# Revit family: Gira_277203
name_source: partatom
category: Elektroinstallationen
revit_build: Autodesk Revit 2017 (Build: 20160225_1515(x64)
units: mm (PartAtom-declared; Revit-internal decimal feet)

## family parameters
Basisbauteil = Fläche
Beim Laden mit Abzugskörper schneiden = Nein
Bemaßung runder Anschluss = Durchmesser verwenden
Beschriftungsausrichtung beibehalten = Nein
Gemeinsam genutzt = Nein
Raumberechnungspunkt = Nein
Teiletyp = Normal

## types (2) — shared parameters
Acoustic signal = Ja
Adjustable differential = Nein
Analogue input = Nein
Antibacterial treatment = Nein
BIM = https://media.stage.bim.site und Tasten.rfa
Beschreibung = Sock.BS Round Pin 5A SH Sys55 PW,Socket outlet British Standard (BS 546) Round Pin 5 A 250 V~ with shutter,System 55, Support ring 71 x 71 mm,pure white glossy,Features:,- With screw terminals.,- For screw mounting only.
Bus connection included = Nein
Bus system KNX = Ja
Bus system KNX radio = Nein
Bus system LON = Nein
Bus system Powernet = Nein
Bus system radio frequent = Nein
Colour = White
Connection = Two-wire
Connection type = Screwed terminal
Control characteristic = Other
Cooling = Nein
Data sheet = https://katalog.gira.de
Degree of protection (IP) = IP20
Eject-mechanism = Nein
Explosion-proof = Nein
External sensor = Nein
Fault current protection = Nein
Für "erschwerte Bedingungen" (nach VDE) (*de-DE) = Nein
GTIN = 4010337079095
HAN = 277203
Halogen free = Ja
Heating = Ja
Hersteller = Gira
Imprint/indication = Without imprint
Insulated mounting = Nein
Label space/information surface = Nein
Lockable = Nein
Material = Plastic
Material quality = Thermoplastic
Measuring range maximum value [m/s] = 30
Measuring range minimum value [m/s] = 5
Model = British Standard
Monitoring window/light outlet = Ja
Mounting method = Flush mounted (plaster)
Nominal current = 5 A
Nominal voltage [Volt] = 250
Number of channels = 3
Number of modules (module system) = 1
Number of units = 1
Operation = Turn
Other bus systems = None
Over voltage protection = Nein
Productwebsite = http://katalog.gira.de
Protective earth pin round = Nein
RAL-number = 9010
RAL-number (akin) = 9010
Rotated central insert = Nein
Scannable symbol / barrier free = Nein
Sensor/feeler type = Other
Special power supply = No special power supply
Suitable for degree of protection (IP) = IP20
Suitable for touch sensor connector for bus system = Nein
Surface finishing = Glossy
Surface protection = Other
Temperature readable = Nein
Thermal feedback = None
Transparent = Nein
Type of fastening = Mounting with screw
Type of power supply = 230 V AC
Typname = Sock.BS Round Pin 5 A SH System 55 p.white
URL = https://www.gira.de
Utilization = Switch/push button
Vorgabe-Ansicht = 1219 mm
Weather station = Nein
With DCF77 = Nein
With built-in USB power supply = Nein
With child-protection = Ja
With display = Nein
With exchangeable lens/symbol = Nein
With function lighting = Nein
With heating = Nein
With hinged lid = Nein
With label area = Nein
With loop through function = Nein
With miniature fuse = Nein
With on/off switch = Nein
With orientation lighting = Nein
With receiver = Nein
With signal lamp = Nein
With sound indicator = Nein
With tap water circuit = Nein
zero-valued in all types: Number of socket outlets switchable

## per-type parameters (varying)
| type | Bauelement |
| Rocker set 3-g in.sp. System 55 clear/p.white | Sys55_Abdeckung_Schalten und Tasten |
| Sys55_Abdeckung_Schalten und Tasten |  |

## geometry (parser evidence)
native form markers: Sweep x6
no freeform markers — native parametric forms only
